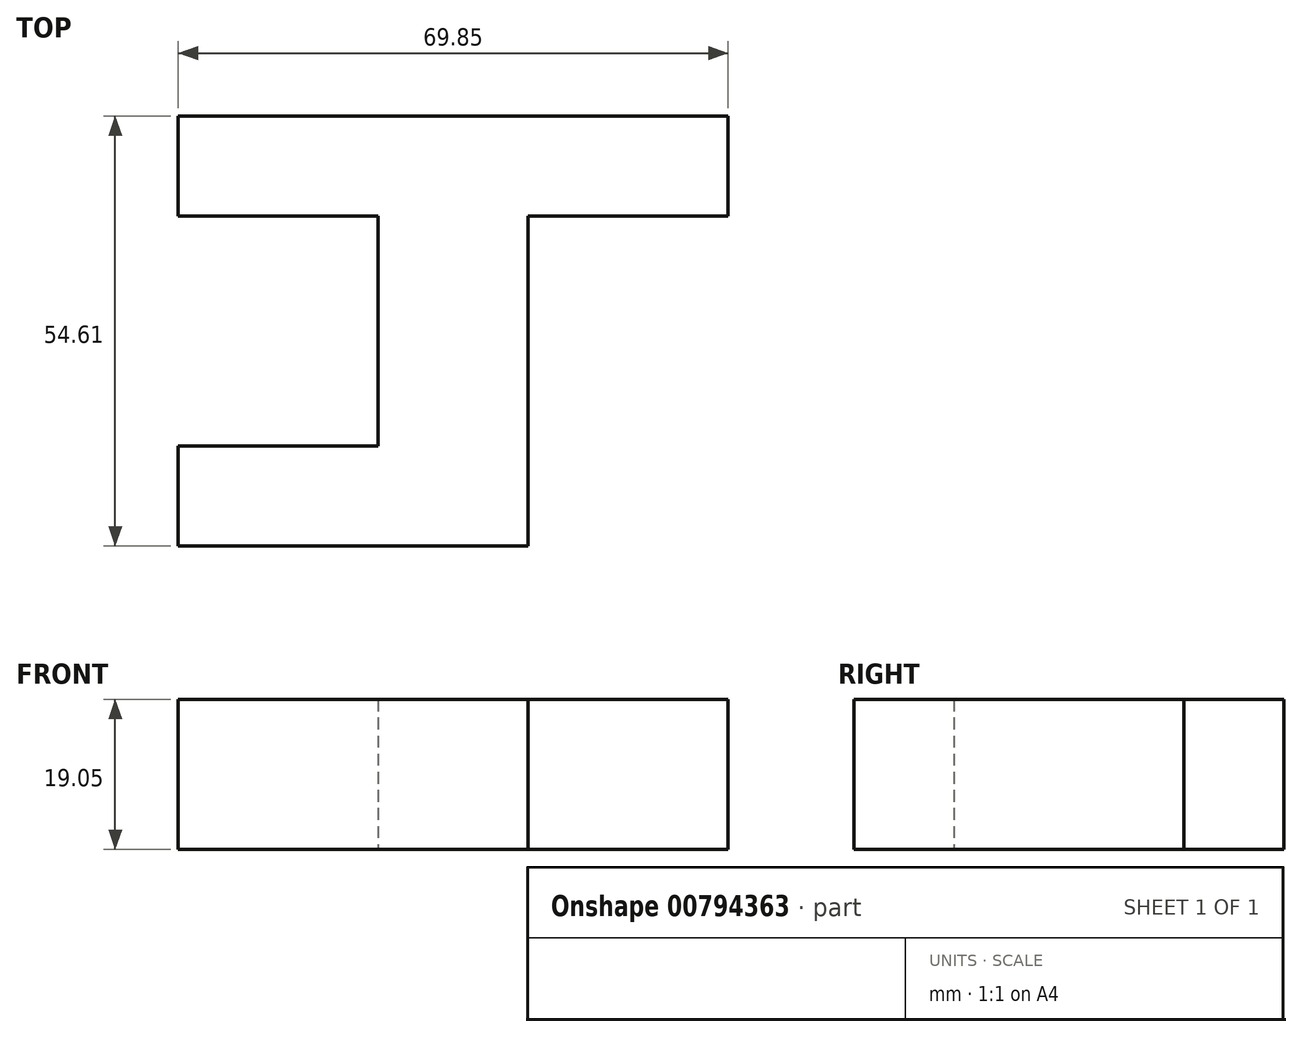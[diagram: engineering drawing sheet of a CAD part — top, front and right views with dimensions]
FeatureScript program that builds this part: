
annotation { "Feature Type Name" : "Feature", "Feature Type Description" : "" }
export const myFeature = defineFeature(function(context is Context, id is Id, definition is map)
    precondition{}
    {
        {
            var Q0;
            Q0=qCreatedBy(makeId("Top.planeOp"),FACE);
            var sketch = newSketch(context, id + "F0", { "sketchPlane" : qUnion([Q0])});
            skLineSegment(sketch, "E0", {"start": v(-39.14, 32.88) * mm, "end": v(30.7, 32.88) * mm});
            skLineSegment(sketch, "E1", {"start": v(-39.14, 32.88) * mm, "end": v(-39.14, 20.18) * mm});
            skLineSegment(sketch, "E2", {"start": v(-39.14, 20.18) * mm, "end": v(-13.74, 20.18) * mm});
            skLineSegment(sketch, "E3", {"start": v(-13.74, 20.18) * mm, "end": v(-13.74, -9.03) * mm});
            skLineSegment(sketch, "E4", {"start": v(-13.74, -9.03) * mm, "end": v(-39.14, -9.03) * mm});
            skLineSegment(sketch, "E5", {"start": v(-39.14, -9.03) * mm, "end": v(-39.14, -21.73) * mm});
            skLineSegment(sketch, "E6", {"start": v(30.7, 32.88) * mm, "end": v(30.7, 20.18) * mm});
            skLineSegment(sketch, "E7", {"start": v(30.7, 20.18) * mm, "end": v(5.3, 20.18) * mm});
            skLineSegment(sketch, "E8", {"start": v(5.3, 20.18) * mm, "end": v(5.3, -21.73) * mm});
            skLineSegment(sketch, "E9", {"start": v(-39.14, -21.73) * mm, "end": v(5.3, -21.73) * mm});
            skSolve(sketch);
        }
        {
            var Q0;
            Q0=makeQuery(id+"F0.imprint","IMPRINT",FACE,{"disambiguationData":[TD([[makeQuery(id+"F0.imprint","IMPRINT",EDGE,{"derivedFrom":sQuery(id+"F0.wireOp",EDGE,"E0")}),-1.0]])]});
            extrude(context, id + "F1", {"entities" : qUnion([Q0]), "depth" : 19.05 * mm, "offsetDistance" : 25.4 * mm});
        }
    });
